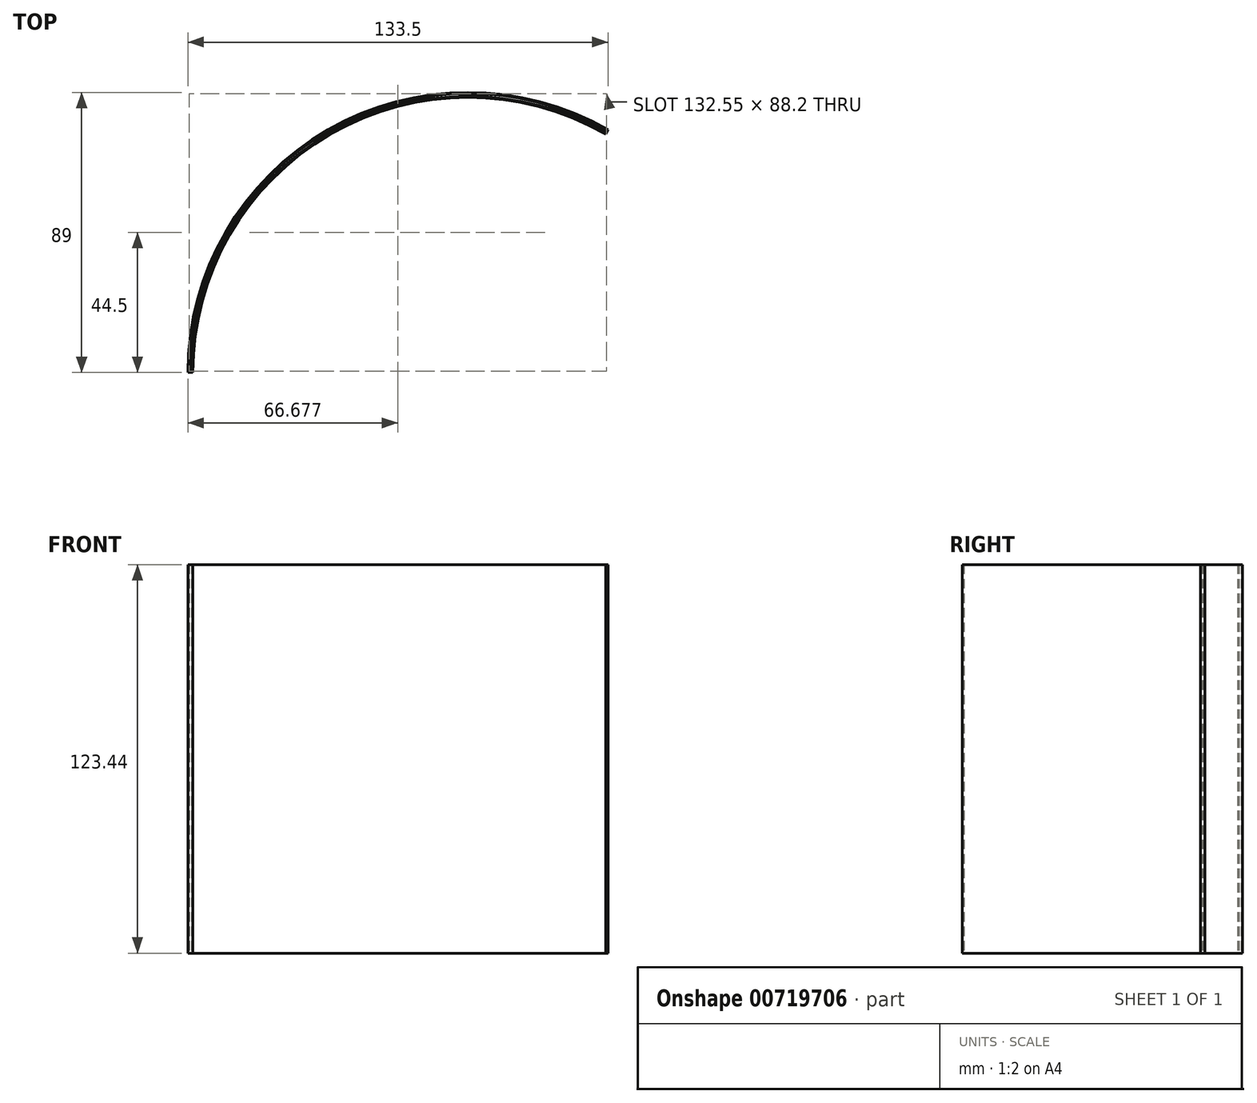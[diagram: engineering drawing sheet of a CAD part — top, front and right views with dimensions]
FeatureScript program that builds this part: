
annotation { "Feature Type Name" : "Feature", "Feature Type Description" : "" }
export const myFeature = defineFeature(function(context is Context, id is Id, definition is map)
    precondition{}
    {
        {
            var Q0;
            Q0=qCreatedBy(makeId("Top.planeOp"),FACE);
            var sketch = newSketch(context, id + "F0", { "sketchPlane" : qUnion([Q0])});
            skArc(sketch, "E0", {"start": v(44.5, 77.08) * mm, "mid": v(-44.5, 77.08) * mm, "end": v(-89, 0) * mm});
            skLineSegment(sketch, "E1", {"start": v(0, 0) * mm, "end": v(44.5, 77.08) * mm, "construction": true});
            skArc(sketch, "E2.0", {"start": v(43.7, 75.7) * mm, "mid": v(-43.7, 75.7) * mm, "end": v(-87.4, 0) * mm});
            skLineSegment(sketch, "E3", {"start": v(43.7, 75.7) * mm, "end": v(44.5, 77.08) * mm});
            skLineSegment(sketch, "E4", {"start": v(-89, 0) * mm, "end": v(-87.4, 0) * mm});
            skArc(sketch, "E5.0", {"start": v(43.95, 76.93) * mm, "mid": v(-44.3, 76.73) * mm, "end": v(-88.6, 0.4) * mm});
            skArc(sketch, "E6.0", {"start": v(43.55, 76.24) * mm, "mid": v(-43.9, 76.04) * mm, "end": v(-87.8, 0.4) * mm});
            skLineSegment(sketch, "E7.0", {"start": v(-88.6, 0.4) * mm, "end": v(-87.8, 0.4) * mm});
            skLineSegment(sketch, "E8.trimOffspring", {"start": v(43.55, 76.24) * mm, "end": v(43.95, 76.93) * mm});
            skSolve(sketch);
        }
        {
            var Q0;
            Q0 = qSketchRegion(id + "F0", true);
            extrude(context, id + "F1", {"entities" : qUnion([Q0]), "depth" : 123.44 * mm, "offsetDistance" : 25 * mm});
        }
    });
